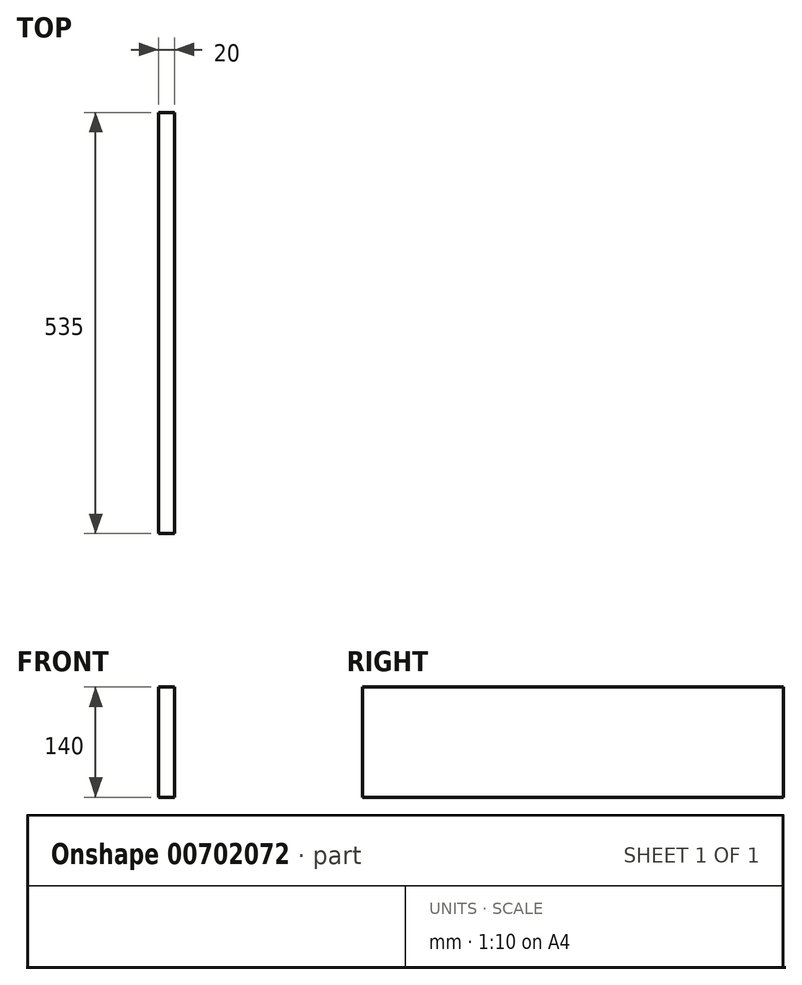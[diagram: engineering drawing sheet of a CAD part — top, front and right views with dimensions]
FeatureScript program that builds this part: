
annotation { "Feature Type Name" : "Feature", "Feature Type Description" : "" }
export const myFeature = defineFeature(function(context is Context, id is Id, definition is map)
    precondition{}
    {
        {
            var Q0;
            Q0=qCreatedBy(makeId("Right.planeOp"),FACE);
            var sketch = newSketch(context, id + "F0", { "sketchPlane" : qUnion([Q0])});
            skLineSegment(sketch, "E0.bottom", {"start": v(0, 0) * mm, "end": v(535, 0) * mm});
            skLineSegment(sketch, "E0.top", {"start": v(0, 140) * mm, "end": v(535, 140) * mm});
            skLineSegment(sketch, "E0.left", {"start": v(0, 0) * mm, "end": v(0, 140) * mm});
            skLineSegment(sketch, "E0.right", {"start": v(535, 0) * mm, "end": v(535, 140) * mm});
            skSolve(sketch);
        }
        {
            var Q0;
            Q0=qSketchRegion(id+"F0",true);
            extrude(context, id + "F1", {"entities" : qUnion([Q0]), "depth" : 20 * mm, "offsetDistance" : 25 * mm});
        }
    });
